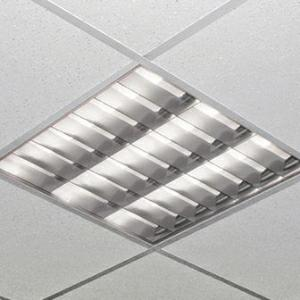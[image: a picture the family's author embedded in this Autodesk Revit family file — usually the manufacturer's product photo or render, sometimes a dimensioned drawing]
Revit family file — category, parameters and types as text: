
# Revit family: 3f_filippi_-_l_320_2mg_3f_filippi_-_28844_-_l_323x10w_led_2mg_596x596
name_source: partatom
category: Lighting Fixtures
units: mm (PartAtom-declared; Revit-internal decimal feet)

## family parameters
Cut with Voids When Loaded = No
Host = Face
Light Source = No
Part Type = Normal
Room Calculation Point = No
Round Connector Dimension = Use Diameter
Shared = No

## types (1)
- 3F Filippi - L 320 2MG (1 x LED, 4287 lm, 34 W, 4000 K)
    Apparent Load = 34 VA
    Approval mark = ENEC
    CIE Flux Codes = 71 98 100 100 100
    Color Rendering = 80
    Color Temperature = 4000 K
    Control Gear = Electronic ballast
    Default Elevation = 1800 mm
    Description = ILLUMINOTECHNICAL
Luminous efficiency 100% (DLOR 100%, ULOR 0%).
Initial luminous flux of the luminaire 4287 lm.
Direct symmetric distribution.
Installation Interdistance Transv.D = 1.27 x hu - Long.D = 1.17 x hu.
Average luminance <1000 cd/m² for radial angles >65°.
Tabular UGR (CIE 117 - 4H-8H; S=0.25H; 70/50/20): RUG 15.1 - 15.5.
Beam angle: 87° - 88°.
Luminous efficacy 126 lm/W.
Lifetime (L93/B10): 30000 h. (tq+25°C)
Lifetime (L90/B10): 50000 h. (tq+25°C)
Lifetime (L85/B10): 80000 h. (tq+25°C)
Lifetime (L80/B10): 100000 h. (tq+25°C)
Sudden decreased luminous flux after 50000 hours: 0% (C0).
Photobiological safety in compliance with IEC/TR 62778: RG0 risk exempt, (IEC 62471).
In compliance with IEC/EN 62722-2-1 - IEC/EN 62717 standards.

SOURCE
3 linear LED modules 10W/840.
Energy efficiency class (UE 2019/2020 - UE 2019/2015): D.
CIE 13.3 Colour rendering index: CRI >80 (R9 <50%).
IES TM-30 Fidelity Index: Rf = 84 Rg = 95.
CCT nominal colour temperature 4000 K.
Colour initial tolerance (MacAdam): SDCM 2.

MECHANICAL
Housing in hot-galvanised steel, painted in white polyester.
2MG parabolic louvre, high efficiency, in specular aluminium with superficial titanium-magnesium treatment, non-iridescent, with transverse blades closed at the top.
Prismatic flat diffusers in transparent methacrylate (PMMA), multilenticular, anti-glare, prismatic outer surface, positioned above the louvre blades.
Film protective against dust and finger marks, adhesive, attached to louvre.
Luminaire with limited surface temperature. - D - (EN 60598-2-24)
Dimensions: 596x596 mm, height 80 mm. Weight 4.21 kg.
IP20 protection degree.
Mechanical strength to impacts IK02 (0.2 joule).
Glow-wire test resistance 650°C.

ELECTRICAL
Halogen Free electronic wiring 230V-50/60Hz, power factor 0.90, THD <25%, constant output current, SELV, class I, 1 driver.
Power of the luminaire 34 W.
CE - IEC 60598-1 - EN 60598-1.
SAFE FLICKER: PstLM=<1 and SVM=<0.4 (IEC TR 61547-1 and IEC TR 63158), to ensure a more comfortable and safe light.
Luminaire compliant with EN 60598-2-22 for power supply from a centralised emergency system CPSS (Central Power Supply System), not incorporated in the luminaire - high risk areas excluded. The default power and flux are 100% in AC and 100% in DC.
Ambient temperature from 0°C to +25°C.
Temperature class T6 max 85°C.
Relative humidity UR: <85%.

INSTALLATION
Lay-in recessed fitting.
On request: pull-up recessed fitting with brackets.
False ceiling carving: 580x580 mm.
All accessories dedicated to this product are available on the Catalog and on our website www.3F-Filippi.com.

APPLICATIONS
In environments with VDTs, managerial offices and staterooms, public offices and schools.

WARNING
Luminaire designed for disposal/recycling at end-of-life.
Replaceable (LED only) light source by a professional. Replaceable control gear by a professional.
    Height = 0 mm  [stored 0 ft]
    Lamp = 1 x LED
    Lamp Light Flux = 4287 lm
    Lamp Power = 34 W
    Lamp count = 1
    Length = 596 mm
    Lifetime = 50000 h
    Luminous efficacy = 126 lm/W
    Manufacturer = 3F Filippi
    ModVariant = No
    Model = 3F Filippi - 28844 - L 323x10W LED 2MG 596x596
    Mounting Place = Ceiling
    Mounting Type = Recessed
    Number of Poles = 1
    OnlyDefault = Yes
    Power Factor = 1
    Product Name = 3F Filippi - L 320 2MG
    Product group = recessed luminaire
    ProductGroupID = 4
    Protection Class = Protection class I
    Protection Degree = IP 20
    RLX_Detail_Level = 1
    RLX_Emergency_Light_Flux = 0 lm
    RLX_Emergency_Type = 0
    RLX_Emergency_Type_DB = No
    RlxData = <blob elided: 93093 chars, md5=bf1c697e>
    Socket = socket
    Standby Power = 0 W
    System Light Flux = 4287 lm
    System Power = 34 W
    Type Comments = Product without accessories
    Type Image = 3ffilippi_28844.jpg
    URL = http://relux.com
    VarID = ---
    Voltage = 0 V
    Weight = 0.00 kg
    Width = 596 mm

note: [stored X ft] marks values corroborated as IEEE doubles in the binary element streams (Revit-internal decimal feet)

## geometry (parser evidence)
native form markers: Blend x4, Sweep x9
no freeform markers — native parametric forms only
